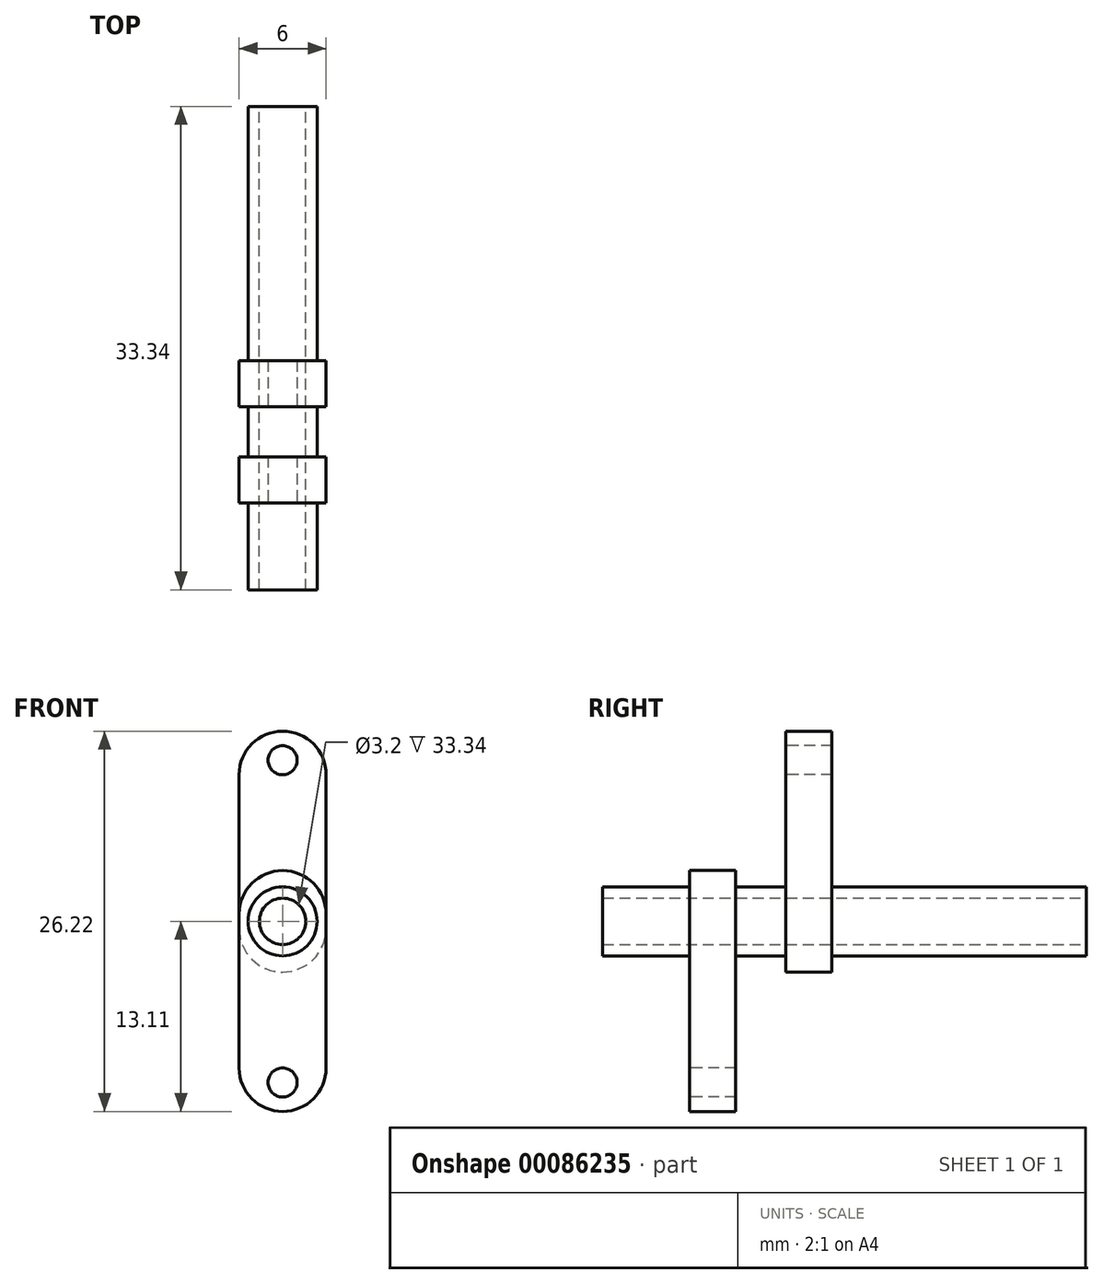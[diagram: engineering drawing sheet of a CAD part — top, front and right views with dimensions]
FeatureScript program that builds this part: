
annotation { "Feature Type Name" : "Feature", "Feature Type Description" : "" }
export const myFeature = defineFeature(function(context is Context, id is Id, definition is map)
    precondition{}
    {
        {
            var Q0;
            Q0=qCreatedBy(makeId("Front.planeOp"),FACE);
            var sketch = newSketch(context, id + "F0", { "sketchPlane" : qUnion([Q0])});
            skCircle(sketch, "E0", {"center": v(0, 0) * mm, "radius": 2.38 * mm});
            skSolve(sketch);
        }
        {
            var Q0;
            Q0 = qSketchRegion(id + "F0", true);
            extrude(context, id + "F1", {"entities" : qUnion([Q0]), "depth" : 33.34 * mm, "offsetDistance" : 25 * mm});
        }
        {
            var Q0;
            Q0=qCreatedBy(makeId("Right.planeOp"),FACE);
            var sketch = newSketch(context, id + "F2", { "sketchPlane" : qUnion([Q0])});
            skLineSegment(sketch, "E1.bottom", {"start": v(-27.34, 3.5) * mm, "end": v(-24.16, 3.5) * mm});
            skLineSegment(sketch, "E1.top", {"start": v(-27.34, -13.11) * mm, "end": v(-24.16, -13.11) * mm});
            skLineSegment(sketch, "E1.left", {"start": v(-27.34, 3.5) * mm, "end": v(-27.34, -13.11) * mm});
            skLineSegment(sketch, "E1.right", {"start": v(-24.16, 3.5) * mm, "end": v(-24.16, -13.11) * mm});
            skLineSegment(sketch, "E2.bottom", {"start": v(-20.71, 13.11) * mm, "end": v(-17.54, 13.11) * mm});
            skLineSegment(sketch, "E2.top", {"start": v(-20.71, -3.5) * mm, "end": v(-17.54, -3.5) * mm});
            skLineSegment(sketch, "E2.left", {"start": v(-20.71, 13.11) * mm, "end": v(-20.71, -3.5) * mm});
            skLineSegment(sketch, "E2.right", {"start": v(-17.54, 13.11) * mm, "end": v(-17.54, -3.5) * mm});
            skLineSegment(sketch, "E3", {"start": v(-27.34, -11.11) * mm, "end": v(-24.16, -11.11) * mm, "construction": true});
            skLineSegment(sketch, "E4", {"start": v(-20.71, 11.11) * mm, "end": v(-17.54, 11.11) * mm, "construction": true});
            skSolve(sketch);
        }
        {
            var Q0;
            Q0=makeQuery(id+"F2.imprint","IMPRINT",FACE,{"disambiguationData":[TD([[makeQuery(id+"F2.imprint","IMPRINT",EDGE,{"derivedFrom":sQuery(id+"F2.wireOp",EDGE,"E1.bottom")}),-1.0]])]});
            var Q1;
            Q1=makeQuery(id+"F2.imprint","IMPRINT",FACE,{"disambiguationData":[TD([[makeQuery(id+"F2.imprint","IMPRINT",EDGE,{"derivedFrom":sQuery(id+"F2.wireOp",EDGE,"E2.bottom")}),-1.0]])]});
            extrude(context, id + "F3", {"entities" : qUnion([Q0, Q1]), "operationType" : NewBodyOperationType.ADD, "depth" : 6 * mm, "offsetDistance" : 25 * mm, "symmetric" : true});
        }
        {
            var Q0;
            Q0=makeQuery(id+"F3.opExtrude","CAP_EDGE",EDGE,{"disambiguationData":[OSD([sQuery(id+"F2.wireOp",EDGE,"E2.bottom")])],"isStart":false});
            var Q1;
            Q1=makeQuery(id+"F3.opExtrude","CAP_EDGE",EDGE,{"disambiguationData":[OSD([sQuery(id+"F2.wireOp",EDGE,"E2.bottom")])],"isStart":true});
            var Q2;
            Q2=makeQuery(id+"F3.opExtrude","CAP_EDGE",EDGE,{"disambiguationData":[OSD([sQuery(id+"F2.wireOp",EDGE,"E2.top")])],"isStart":false});
            var Q3;
            Q3=makeQuery(id+"F3.opExtrude","CAP_EDGE",EDGE,{"disambiguationData":[OSD([sQuery(id+"F2.wireOp",EDGE,"E2.top")])],"isStart":true});
            var Q4;
            Q4=makeQuery(id+"F3.opExtrude","CAP_EDGE",EDGE,{"disambiguationData":[OSD([sQuery(id+"F2.wireOp",EDGE,"E1.bottom")])],"isStart":true});
            var Q5;
            Q5=makeQuery(id+"F3.opExtrude","CAP_EDGE",EDGE,{"disambiguationData":[OSD([sQuery(id+"F2.wireOp",EDGE,"E1.bottom")])],"isStart":false});
            var Q6;
            Q6=makeQuery(id+"F3.opExtrude","CAP_EDGE",EDGE,{"disambiguationData":[OSD([sQuery(id+"F2.wireOp",EDGE,"E1.top")])],"isStart":false});
            var Q7;
            Q7=makeQuery(id+"F3.opExtrude","CAP_EDGE",EDGE,{"disambiguationData":[OSD([sQuery(id+"F2.wireOp",EDGE,"E1.top")])],"isStart":true});
            fillet(context, id + "F4", {"entities" : qUnion([Q0, Q1, Q2, Q3, Q4, Q5, Q6, Q7]), "radius" : 3 * mm, "tangentPropagation" : true, "allowEdgeOverflow" : false});
        }
        {
            var Q0;
            Q0=makeQuery(id+"F1.opExtrude","CAP_FACE",FACE,{"disambiguationData":[OSD([sQuery(id+"F0.wireOp",EDGE,"E0")])],"isStart":true});
            var sketch = newSketch(context, id + "F5", { "sketchPlane" : qUnion([Q0])});
            skCircle(sketch, "E5", {"center": v(0, 0) * mm, "radius": 1.6 * mm});
            skSolve(sketch);
        }
        {
            var Q0;
            Q0 = qSketchRegion(id + "F5", true);
            extrude(context, id + "F6", {"entities" : qUnion([Q0]), "operationType" : NewBodyOperationType.REMOVE, "endBound" : BoundingType.THROUGH_ALL, "oppositeDirection" : true, "depth" : 25 * mm, "offsetDistance" : 25 * mm});
        }
        {
            var Q0;
            Q0=makeQuery(id+"F3.opExtrude","SWEPT_FACE",FACE,{"disambiguationData":[OSD([sQuery(id+"F2.wireOp",EDGE,"E1.left")])]});
            var sketch = newSketch(context, id + "F7", { "sketchPlane" : qUnion([Q0])});
            skCircle(sketch, "E6", {"center": v(0, -11.11) * mm, "radius": 1 * mm});
            skCircle(sketch, "E7", {"center": v(0, 11.11) * mm, "radius": 1 * mm});
            skLineSegment(sketch, "E8", {"start": v(0, 0) * mm, "end": v(17.53, 0) * mm, "construction": true});
            skSolve(sketch);
        }
        {
            var Q0;
            Q0 = qSketchRegion(id + "F7", true);
            extrude(context, id + "F8", {"entities" : qUnion([Q0]), "operationType" : NewBodyOperationType.REMOVE, "endBound" : BoundingType.THROUGH_ALL, "oppositeDirection" : true, "depth" : 25 * mm, "offsetDistance" : 25 * mm});
        }
    });
